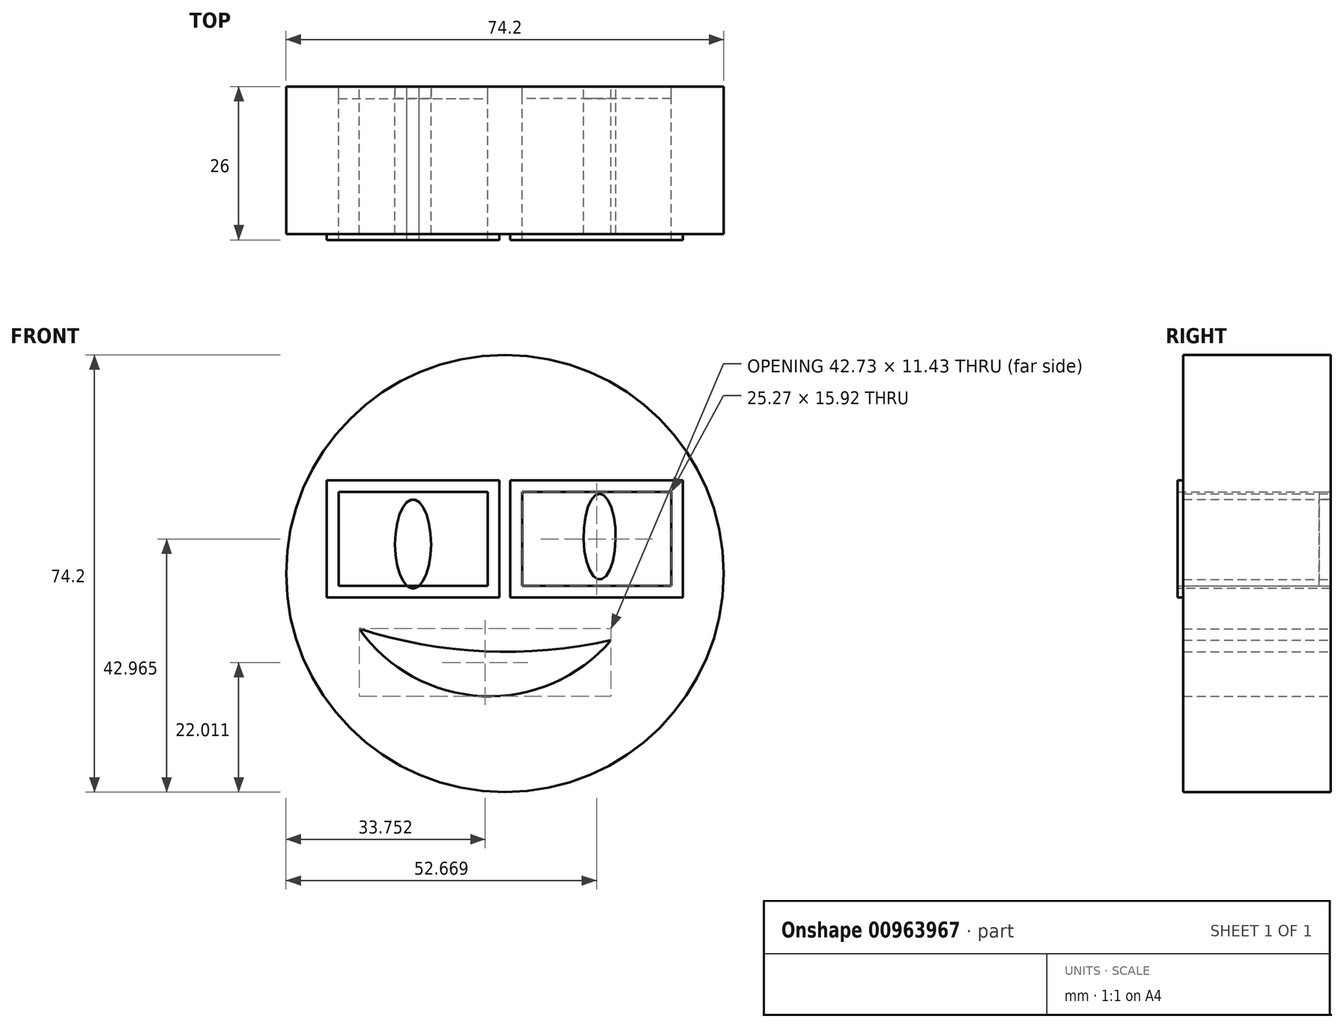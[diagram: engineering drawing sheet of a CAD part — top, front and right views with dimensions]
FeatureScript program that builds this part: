
annotation { "Feature Type Name" : "Feature", "Feature Type Description" : "" }
export const myFeature = defineFeature(function(context is Context, id is Id, definition is map)
    precondition{}
    {
        {
            var Q0;
            Q0=qCreatedBy(makeId("Front.planeOp"),FACE);
            var sketch = newSketch(context, id + "F0", { "sketchPlane" : qUnion([Q0])});
            skCircle(sketch, "E0", {"center": v(0, 0) * mm, "radius": 37.1 * mm});
            skLineSegment(sketch, "E1", {"start": v(-28.2, 13.82) * mm, "end": v(-2.93, 13.82) * mm});
            skLineSegment(sketch, "E2", {"start": v(-2.93, 13.82) * mm, "end": v(-2.93, -2.1) * mm});
            skLineSegment(sketch, "E3", {"start": v(-28.2, 13.82) * mm, "end": v(-28.2, -2.1) * mm});
            skLineSegment(sketch, "E4", {"start": v(-28.2, -2.1) * mm, "end": v(-2.93, -2.1) * mm});
            skLineSegment(sketch, "E5.MirrorCS", {"start": v(28.2, 13.82) * mm, "end": v(2.93, 13.82) * mm});
            skLineSegment(sketch, "E6.MirrorCS", {"start": v(2.93, 13.82) * mm, "end": v(2.93, -2.1) * mm});
            skLineSegment(sketch, "E7.MirrorCS", {"start": v(28.2, -2.1) * mm, "end": v(2.93, -2.1) * mm});
            skLineSegment(sketch, "E8.MirrorCS", {"start": v(28.2, 13.82) * mm, "end": v(28.2, -2.1) * mm});
            skArc(sketch, "E9", {"start": v(-24.71, -9.37) * mm, "mid": v(-3.48, -13.2) * mm, "end": v(18.02, -11.33) * mm});
            skArc(sketch, "E10", {"start": v(-24.71, -9.37) * mm, "mid": v(-3.83, -20.8) * mm, "end": v(18.02, -11.33) * mm});
            skEllipse(sketch, "E11", {"center": v(-15.57, 5.01) * mm, "majorRadius": 7.54 * mm, "minorRadius": 3.05 * mm, "majorAxis": v(0, 1)});
            skPoint(sketch, "E11.centerSnap0", {"position": v(-15.57, -2.1) * mm});
            skEllipse(sketch, "E12", {"center": v(16.06, 6.25) * mm, "majorRadius": 7.28 * mm, "minorRadius": 2.72 * mm, "majorAxis": v(0, 1)});
            skLineSegment(sketch, "E13.0", {"start": v(-30.2, 15.82) * mm, "end": v(-0.93, 15.82) * mm});
            skLineSegment(sketch, "E13.2", {"start": v(-30.2, -4.1) * mm, "end": v(-0.93, -4.1) * mm});
            skLineSegment(sketch, "E13.3", {"start": v(-0.93, 15.82) * mm, "end": v(-0.93, -4.1) * mm});
            skLineSegment(sketch, "E14", {"start": v(-30.2, 15.82) * mm, "end": v(-30.2, -4.1) * mm});
            skLineSegment(sketch, "E15.MirrorCS", {"start": v(30.2, 15.82) * mm, "end": v(0.93, 15.82) * mm});
            skLineSegment(sketch, "E16.MirrorCS", {"start": v(0.93, 15.82) * mm, "end": v(0.93, -4.1) * mm});
            skLineSegment(sketch, "E17.MirrorCS", {"start": v(30.2, -4.1) * mm, "end": v(0.93, -4.1) * mm});
            skLineSegment(sketch, "E18.MirrorCS", {"start": v(30.2, 15.82) * mm, "end": v(30.2, -4.1) * mm});
            skSolve(sketch);
        }
        {
            var Q0;
            Q0=makeQuery(id+"F0.imprint","IMPRINT",FACE,{"disambiguationData":[TD([[makeQuery(id+"F0.imprint","IMPRINT",EDGE,{"derivedFrom":sQuery(id+"F0.wireOp",EDGE,"E0")}),1.0]])]});
            extrude(context, id + "F1", {"entities" : qUnion([Q0]), "depth" : 25 * mm, "offsetDistance" : 25 * mm});
        }
        {
            var Q0;
            Q0=makeQuery(id+"F0.imprint","IMPRINT",FACE,{"disambiguationData":[TD([[makeQuery(id+"F0.imprint","IMPRINT",EDGE,{"derivedFrom":sQuery(id+"F0.wireOp",EDGE,"E1")}),1.0]])]});
            var Q1;
            Q1=makeQuery(id+"F0.imprint","IMPRINT",FACE,{"disambiguationData":[TD([[makeQuery(id+"F0.imprint","IMPRINT",EDGE,{"derivedFrom":sQuery(id+"F0.wireOp",EDGE,"E5.MirrorCS")}),-1.0]])]});
            extrude(context, id + "F2", {"entities" : qUnion([Q0, Q1]), "operationType" : NewBodyOperationType.ADD, "depth" : 26 * mm, "offsetDistance" : 25 * mm});
        }
        {
            var Q0;
            {var subQ0=sQuery(id+"F0.wireOp",EDGE,"E11");var subQ1=sQuery(id+"F0.wireOp",EDGE,"E4");var subQ2=makeQuery(id+"F0.imprint","INTERSECT",VERTEX,{"disambiguationData":[OD(0.0)],"derivedFrom":[subQ1,subQ0]});Q0=makeQuery(id+"F0.imprint","IMPRINT",FACE,{"disambiguationData":[TD([[makeQuery(id+"F0.imprint","IMPRINT",EDGE,{"disambiguationData":[TD([[subQ2,-1.0]])],"derivedFrom":subQ1}),1.0]])]});}
            var Q1;
            Q1=makeQuery(id+"F0.imprint","IMPRINT",FACE,{"disambiguationData":[TD([[makeQuery(id+"F0.imprint","IMPRINT",EDGE,{"derivedFrom":sQuery(id+"F0.wireOp",EDGE,"E12")}),1.0]])]});
            extrude(context, id + "F3", {"entities" : qUnion([Q0, Q1]), "depth" : 25 * mm, "offsetDistance" : 25 * mm});
        }
        {
            var Q0;
            Q0=makeQuery(id+"F0.imprint","IMPRINT",FACE,{"disambiguationData":[TD([[makeQuery(id+"F0.imprint","IMPRINT",EDGE,{"derivedFrom":sQuery(id+"F0.wireOp",EDGE,"E5.MirrorCS")}),1.0]])]});
            var Q1;
            Q1=makeQuery(id+"F0.imprint","IMPRINT",FACE,{"disambiguationData":[TD([[makeQuery(id+"F0.imprint","IMPRINT",EDGE,{"derivedFrom":sQuery(id+"F0.wireOp",EDGE,"E1")}),-1.0]])]});
            extrude(context, id + "F4", {"entities" : qUnion([Q0, Q1]), "depth" : 2 * mm, "offsetDistance" : 25 * mm});
        }
    });
